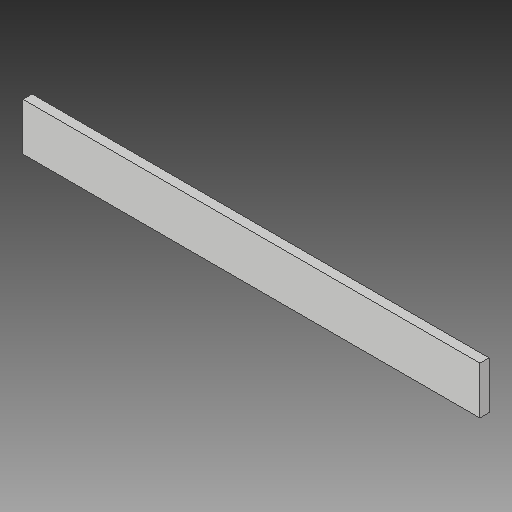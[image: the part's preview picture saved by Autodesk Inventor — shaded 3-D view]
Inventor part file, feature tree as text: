
AUTODESK INVENTOR PART (.ipt)
format: ipt  version: 2019 (Build 230136000, 136)  size: 98,304 bytes
history: native  units: mm
features: extrude x1, sketch x1
ambient origin geometry x8: Origin, YZ Plane, XZ Plane, XY Plane, X Axis, Y Axis, Z Axis, Center Point
bodies: Solid1 (feature_tree)
feature tree (2):
  extrude  "Extrusion1"  Depth=500.0mm
  sketch  "Sketch1"  dims[d0=5.5mm d1=500.0mm d2=52.0mm d3=10.0mm d4=0.0mm]
